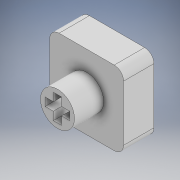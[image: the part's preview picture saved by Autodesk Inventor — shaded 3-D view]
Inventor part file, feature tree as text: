
AUTODESK INVENTOR PART (.ipt)
format: ipt  version: 2022 (Build 260153000, 153)  size: 260,608 bytes
history: native  units: in
note: dims shown in document units (in); Inventor stores cm internally (conversion verified against a paired STEP export)
features: sketch x5, extrude x3, plane x1, projected_geometry x1
ambient origin geometry x8: Origin, YZ Plane, XZ Plane, XY Plane, X Axis, Y Axis, Z Axis, Center Point
bodies: Body1 (feature_tree)
feature tree (10):
  sketch  "Sketch1"  dims[d3=0.2205in d4=0.1594in]
  plane  "Work Plane1"
  sketch  "Sketch2"  dims[d5=0.0531in d6=0.1594in]
  extrude  "Extrusion3"  Depth=0.1594in
  extrude  "Extrusion4"  Depth=0.1594in
  sketch  "Sketch4"  dims[d12=0.1969in d13=0.0in]
  sketch  "Sketch5"  dims[d14=0.2205in d15=0.1594in d16=0.0531in d17=0.1594in d18=0.0531in d19=0.189in d20=0.0in d21=0.0892in d22=0.2693in d23=0.0354in d24=0.0in]
  extrude  "Extrusion5"  Depth=0.5016in
  projected_geometry  "Projected Loop1"
  sketch  "Sketch3"  dims[d7=0.0531in d10=0.5016in]
